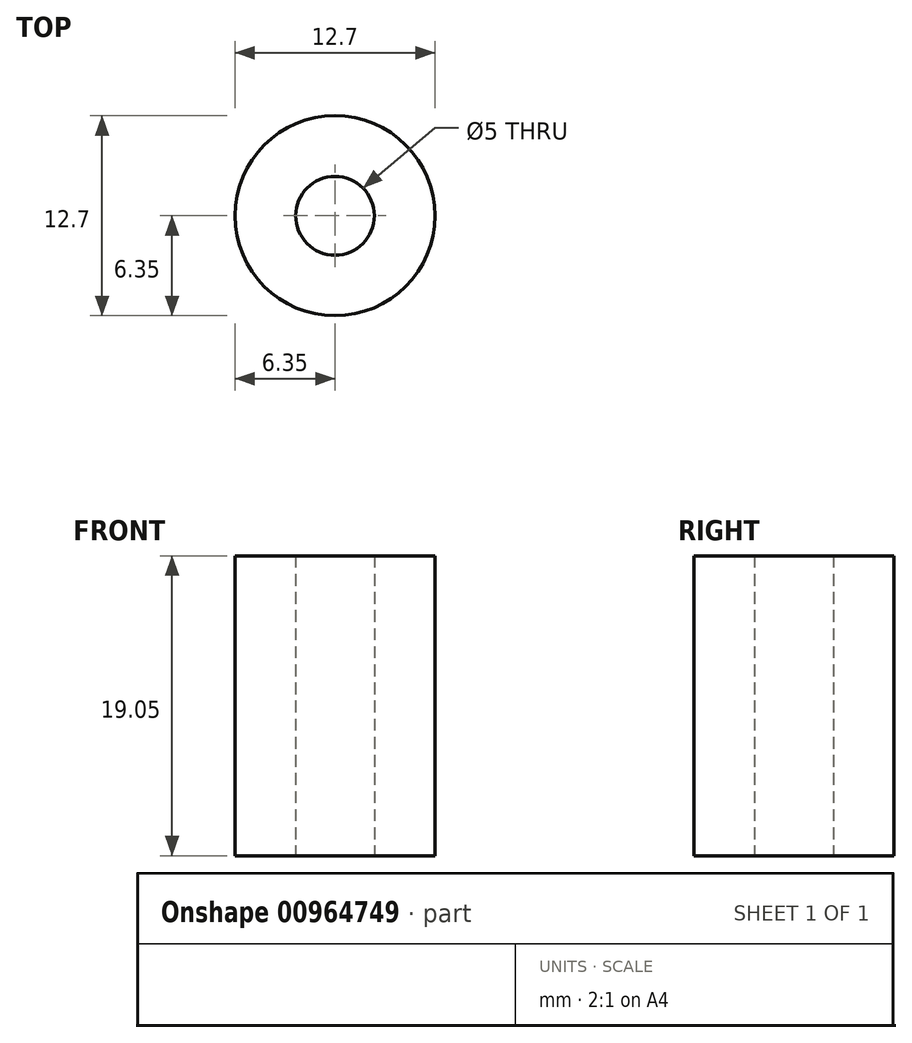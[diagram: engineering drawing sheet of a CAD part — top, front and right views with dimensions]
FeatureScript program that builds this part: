
annotation { "Feature Type Name" : "Feature", "Feature Type Description" : "" }
export const myFeature = defineFeature(function(context is Context, id is Id, definition is map)
    precondition{}
    {
        {
            var Q0;
            Q0=qCreatedBy(makeId("Top.planeOp"),FACE);
            var sketch = newSketch(context, id + "F0", { "sketchPlane" : qUnion([Q0])});
            skCircle(sketch, "E0", {"center": v(0, 0) * mm, "radius": 6.35 * mm});
            skCircle(sketch, "E1", {"center": v(0, 0) * mm, "radius": 2.5 * mm});
            skSolve(sketch);
        }
        {
            var Q0;
            Q0 = qSketchRegion(id + "F0", true);
            extrude(context, id + "F1", {"entities" : qUnion([Q0]), "depth" : 19.05 * mm, "offsetDistance" : 25.4 * mm});
        }
    });
